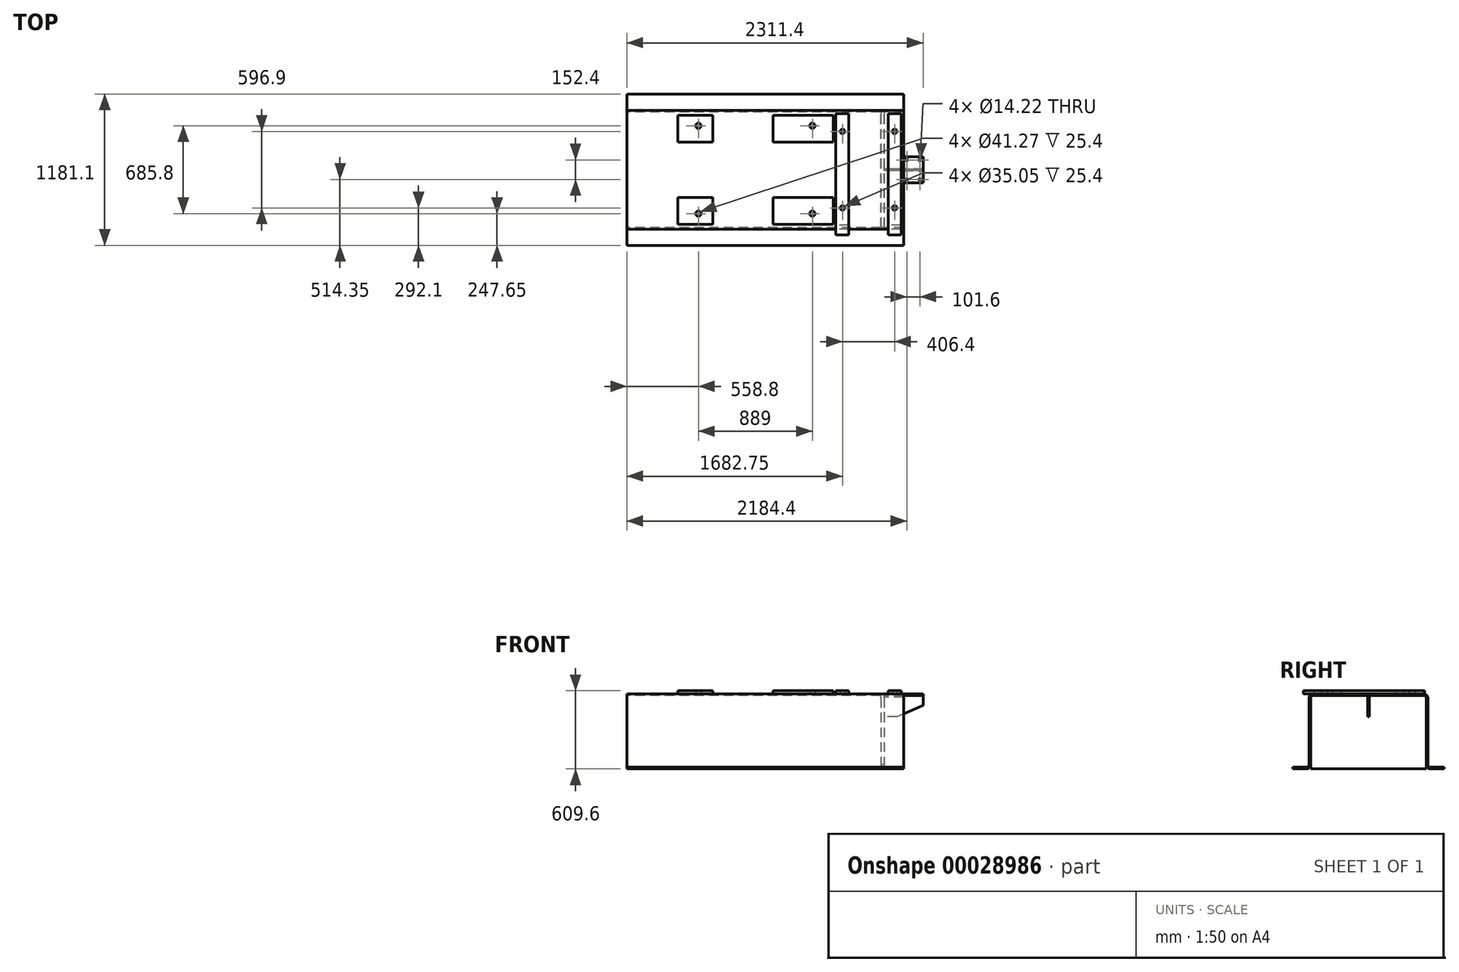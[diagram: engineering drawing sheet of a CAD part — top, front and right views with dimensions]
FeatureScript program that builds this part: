
annotation { "Feature Type Name" : "Feature", "Feature Type Description" : "" }
export const myFeature = defineFeature(function(context is Context, id is Id, definition is map)
    precondition{}
    {
        {
            var Q0;
            Q0=qCreatedBy(makeId("Right.planeOp"),FACE);
            var sketch = newSketch(context, id + "F0", { "sketchPlane" : qUnion([Q0])});
            skLineSegment(sketch, "E0", {"start": v(0, 584.2) * mm, "end": v(0, -94.25) * mm, "construction": true});
            skLineSegment(sketch, "E1", {"start": v(-590.55, 0) * mm, "end": v(129.12, 0) * mm, "construction": true});
            skLineSegment(sketch, "E2.0", {"start": v(-590.55, 88.53) * mm, "end": v(-590.55, -94.25) * mm, "construction": true});
            skPoint(sketch, "E3.orphan", {"position": v(-130.91, 0) * mm});
            skLineSegment(sketch, "E4.0", {"start": v(-590.55, 12.7) * mm, "end": v(129.12, 12.7) * mm, "construction": true});
            skLineSegment(sketch, "E5.0", {"start": v(-590.55, 584.2) * mm, "end": v(129.12, 584.2) * mm, "construction": true});
            skPoint(sketch, "E6.orphan", {"position": v(0, 88.53) * mm});
            skLineSegment(sketch, "E7.0", {"start": v(-463.55, 584.2) * mm, "end": v(-463.55, -94.25) * mm, "construction": true});
            skLineSegment(sketch, "E8.0", {"start": v(-450.85, 584.2) * mm, "end": v(-450.85, -94.25) * mm, "construction": true});
            skLineSegment(sketch, "E9.0", {"start": v(-590.55, 571.5) * mm, "end": v(129.12, 571.5) * mm, "construction": true});
            skLineSegment(sketch, "E10", {"start": v(-590.55, 12.7) * mm, "end": v(-482.6, 12.7) * mm});
            skLineSegment(sketch, "E11", {"start": v(-463.55, 31.75) * mm, "end": v(-463.55, 552.45) * mm});
            skLineSegment(sketch, "E12", {"start": v(0, 584.2) * mm, "end": v(-431.8, 584.2) * mm});
            skLineSegment(sketch, "E13", {"start": v(0, 571.5) * mm, "end": v(-431.8, 571.5) * mm});
            skLineSegment(sketch, "E14", {"start": v(-450.85, 552.45) * mm, "end": v(-450.85, 31.75) * mm});
            skLineSegment(sketch, "E15", {"start": v(-482.6, 0) * mm, "end": v(-590.55, 0) * mm});
            skLineSegment(sketch, "E16", {"start": v(-590.55, 12.7) * mm, "end": v(-590.55, 0) * mm});
            skPoint(sketch, "E17.visualSharp", {"position": v(-463.55, 12.7) * mm});
            skArc(sketch, "E17.filletArc", {"start": v(-482.6, 12.7) * mm, "mid": v(-469.13, 18.28) * mm, "end": v(-463.55, 31.75) * mm});
            skPoint(sketch, "E18.visualSharp", {"position": v(-450.85, 571.5) * mm});
            skArc(sketch, "E18.filletArc", {"start": v(-431.8, 571.5) * mm, "mid": v(-445.27, 565.92) * mm, "end": v(-450.85, 552.45) * mm});
            skPoint(sketch, "E19.visualSharp", {"position": v(-463.55, 584.2) * mm});
            skArc(sketch, "E19.filletArc", {"start": v(-431.8, 584.2) * mm, "mid": v(-454.25, 574.9) * mm, "end": v(-463.55, 552.45) * mm});
            skPoint(sketch, "E20.visualSharp", {"position": v(-450.85, 0) * mm});
            skArc(sketch, "E20.filletArc", {"start": v(-482.6, 0) * mm, "mid": v(-460.15, 9.3) * mm, "end": v(-450.85, 31.75) * mm});
            skArc(sketch, "E21.MirrorCS", {"start": v(431.8, 571.5) * mm, "mid": v(445.27, 565.92) * mm, "end": v(450.85, 552.45) * mm});
            skArc(sketch, "E22.MirrorCS", {"start": v(431.8, 584.2) * mm, "mid": v(454.25, 574.9) * mm, "end": v(463.55, 552.45) * mm});
            skLineSegment(sketch, "E23.MirrorCS", {"start": v(450.85, 577.85) * mm, "end": v(450.85, 31.75) * mm});
            skPoint(sketch, "E24.MirrorP", {"position": v(450.85, 571.5) * mm});
            skLineSegment(sketch, "E25.MirrorCS", {"start": v(0, 584.2) * mm, "end": v(431.8, 584.2) * mm});
            skLineSegment(sketch, "E26.MirrorCS", {"start": v(463.55, 31.75) * mm, "end": v(463.55, 552.45) * mm});
            skLineSegment(sketch, "E27.MirrorCS", {"start": v(0, 571.5) * mm, "end": v(431.8, 571.5) * mm});
            skPoint(sketch, "E28.MirrorP", {"position": v(463.55, 584.2) * mm});
            skLineSegment(sketch, "E29.MirrorCS", {"start": v(450.85, 552.45) * mm, "end": v(450.85, 31.75) * mm});
            skLineSegment(sketch, "E30.MirrorCS", {"start": v(457.2, 571.5) * mm, "end": v(-129.12, 571.5) * mm});
            skLineSegment(sketch, "E31.MirrorCS", {"start": v(590.55, 12.7) * mm, "end": v(590.55, 0) * mm});
            skArc(sketch, "E32.MirrorCS", {"start": v(482.6, 12.7) * mm, "mid": v(469.13, 18.28) * mm, "end": v(463.55, 31.75) * mm});
            skArc(sketch, "E33.MirrorCS", {"start": v(482.6, 0) * mm, "mid": v(460.15, 9.3) * mm, "end": v(450.85, 31.75) * mm});
            skPoint(sketch, "E34.MirrorP", {"position": v(450.85, 0) * mm});
            skPoint(sketch, "E35.MirrorP", {"position": v(463.55, 12.7) * mm});
            skLineSegment(sketch, "E36.MirrorCS", {"start": v(590.55, 0) * mm, "end": v(482.6, 0) * mm});
            skLineSegment(sketch, "E37.MirrorCS", {"start": v(482.6, 0) * mm, "end": v(590.55, 0) * mm});
            skLineSegment(sketch, "E38.MirrorCS", {"start": v(590.55, 88.53) * mm, "end": v(590.55, -94.25) * mm});
            skLineSegment(sketch, "E39.MirrorCS", {"start": v(590.55, 12.7) * mm, "end": v(482.6, 12.7) * mm});
            skLineSegment(sketch, "E40.MirrorCS", {"start": v(463.55, 552.45) * mm, "end": v(463.55, 31.75) * mm});
            skLineSegment(sketch, "E41.MirrorCS", {"start": v(590.55, 12.7) * mm, "end": v(463.55, 12.7) * mm});
            skLineSegment(sketch, "E42.MirrorCS", {"start": v(450.85, 584.2) * mm, "end": v(450.85, 31.75) * mm});
            skLineSegment(sketch, "E43.trimOffspring", {"start": v(129.12, 12.7) * mm, "end": v(-129.12, 12.7) * mm});
            skLineSegment(sketch, "E44.trimOffspring", {"start": v(463.55, 12.7) * mm, "end": v(463.55, 6.35) * mm});
            skLineSegment(sketch, "E45.trimOffspring", {"start": v(129.12, 0) * mm, "end": v(-129.12, 0) * mm});
            skPoint(sketch, "E46.trimOffspring.end.orphan", {"position": v(463.55, -94.25) * mm});
            skPoint(sketch, "E47.trimOffspring.end.orphan", {"position": v(450.85, -94.25) * mm});
            skLineSegment(sketch, "E48.trimOffspring", {"start": v(431.8, 584.2) * mm, "end": v(-129.12, 584.2) * mm});
            skPoint(sketch, "E49.orphan", {"position": v(450.85, 584.2) * mm});
            skPoint(sketch, "E50.orphan", {"position": v(590.55, 571.5) * mm});
            skLineSegment(sketch, "E51.trimOffspring", {"start": v(463.55, 552.45) * mm, "end": v(463.55, 6.35) * mm});
            skPoint(sketch, "E52.MirrorCS.start.orphan", {"position": v(590.55, 584.2) * mm});
            skSolve(sketch);
        }
        {
            var Q0;
            Q0 = qSketchRegion(id + "F0", true);
            extrude(context, id + "F1", {"entities" : qUnion([Q0]), "endBound" : BoundingType.SYMMETRIC, "depth" : 2159 * mm});
        }
        {
            var Q0;
            Q0=makeQuery(id+"F1.opExtrude","SWEPT_FACE",FACE,{"disambiguationData":[OSD([sQuery(id+"F0.wireOp",EDGE,"E12"),sQuery(id+"F0.wireOp",EDGE,"E48.trimOffspring")])]});
            var sketch = newSketch(context, id + "F2", { "sketchPlane" : qUnion([Q0])});
            skLineSegment(sketch, "E53", {"start": v(-1403.71, 0) * mm, "end": v(1616.58, 0) * mm, "construction": true});
            skLineSegment(sketch, "E54.0", {"start": v(-1403.71, 215.9) * mm, "end": v(1616.58, 215.9) * mm, "construction": true});
            skLineSegment(sketch, "E55.0", {"start": v(-1403.71, 425.45) * mm, "end": v(1616.58, 425.45) * mm, "construction": true});
            skLineSegment(sketch, "E56.0", {"start": v(806.45, 431.8) * mm, "end": v(806.45, -431.8) * mm, "construction": true});
            skLineSegment(sketch, "E57.0", {"start": v(-76.2, 431.8) * mm, "end": v(-76.2, -431.8) * mm, "construction": true});
            skLineSegment(sketch, "E58.0", {"start": v(60.45, 431.8) * mm, "end": v(60.45, -431.8) * mm, "construction": true});
            skLineSegment(sketch, "E59.0", {"start": v(530.35, 431.8) * mm, "end": v(530.35, -431.8) * mm, "construction": true});
            skLineSegment(sketch, "E60.0", {"start": v(-409.45, 431.8) * mm, "end": v(-409.45, -431.8) * mm, "construction": true});
            skLineSegment(sketch, "E61.0", {"start": v(-682.5, 431.8) * mm, "end": v(-682.5, -431.8) * mm, "construction": true});
            skLineSegment(sketch, "E62.bottom", {"start": v(-682.5, 425.45) * mm, "end": v(-409.45, 425.45) * mm});
            skLineSegment(sketch, "E62.top", {"start": v(-682.5, 215.9) * mm, "end": v(-409.45, 215.9) * mm});
            skLineSegment(sketch, "E62.left", {"start": v(-682.5, 425.45) * mm, "end": v(-682.5, 215.9) * mm});
            skLineSegment(sketch, "E62.right", {"start": v(-409.45, 425.45) * mm, "end": v(-409.45, 215.9) * mm});
            skLineSegment(sketch, "E63.bottom", {"start": v(530.35, 425.45) * mm, "end": v(60.45, 425.45) * mm});
            skLineSegment(sketch, "E63.top", {"start": v(530.35, 215.9) * mm, "end": v(60.45, 215.9) * mm});
            skLineSegment(sketch, "E63.left", {"start": v(530.35, 425.45) * mm, "end": v(530.35, 215.9) * mm});
            skLineSegment(sketch, "E63.right", {"start": v(60.45, 425.45) * mm, "end": v(60.45, 215.9) * mm});
            skLineSegment(sketch, "E64.0", {"start": v(-520.7, 431.8) * mm, "end": v(-520.7, -431.8) * mm, "construction": true});
            skLineSegment(sketch, "E65.0", {"start": v(-1403.71, 342.9) * mm, "end": v(1616.58, 342.9) * mm, "construction": true});
            skLineSegment(sketch, "E66.MirrorCS", {"start": v(368.3, 431.8) * mm, "end": v(368.3, -431.8) * mm, "construction": true});
            skCircle(sketch, "E67", {"center": v(-520.7, 342.9) * mm, "radius": 20.64 * mm});
            skCircle(sketch, "E68", {"center": v(368.3, 342.9) * mm, "radius": 20.64 * mm});
            skCircle(sketch, "E69.MirrorC", {"center": v(-520.7, -342.9) * mm, "radius": 20.64 * mm});
            skCircle(sketch, "E70.MirrorC", {"center": v(368.3, -342.9) * mm, "radius": 20.64 * mm});
            skLineSegment(sketch, "E71.MirrorCS", {"start": v(-682.5, -425.45) * mm, "end": v(-409.45, -425.45) * mm});
            skLineSegment(sketch, "E72.MirrorCS", {"start": v(-682.5, -215.9) * mm, "end": v(-409.45, -215.9) * mm});
            skLineSegment(sketch, "E73.MirrorCS", {"start": v(530.35, -425.45) * mm, "end": v(530.35, -215.9) * mm});
            skLineSegment(sketch, "E74.MirrorCS", {"start": v(-682.5, -425.45) * mm, "end": v(-682.5, -215.9) * mm});
            skLineSegment(sketch, "E75.MirrorCS", {"start": v(-409.45, -425.45) * mm, "end": v(-409.45, -215.9) * mm});
            skLineSegment(sketch, "E76.MirrorCS", {"start": v(60.45, -425.45) * mm, "end": v(60.45, -215.9) * mm});
            skLineSegment(sketch, "E77.MirrorCS", {"start": v(530.35, -425.45) * mm, "end": v(60.45, -425.45) * mm});
            skLineSegment(sketch, "E78.MirrorCS", {"start": v(530.35, -215.9) * mm, "end": v(60.45, -215.9) * mm});
            skSolve(sketch);
        }
        {
            var Q0;
            Q0 = qSketchRegion(id + "F2", true);
            extrude(context, id + "F3", {"entities" : qUnion([Q0]), "operationType" : NewBodyOperationType.ADD, "depth" : 25.4 * mm});
        }
        {
            var Q0;
            Q0=makeQuery(id+"F2.imprint","IMPRINT",FACE,{"disambiguationData":[TD([[makeQuery(id+"F2.imprint","IMPRINT",EDGE,{"derivedFrom":sQuery(id+"F2.wireOp",EDGE,"E62.bottom")}),1.0]])]});
            var sketch = newSketch(context, id + "F4", { "sketchPlane" : qUnion([Q0])});
            skLineSegment(sketch, "E79.0", {"start": v(806.45, 438.15) * mm, "end": v(806.45, -431.8) * mm, "construction": true});
            skLineSegment(sketch, "E80.0", {"start": v(-1403.71, 0) * mm, "end": v(1616.58, 0) * mm, "construction": true});
            skLineSegment(sketch, "E81.0", {"start": v(652.53, 438.15) * mm, "end": v(652.53, -508) * mm, "construction": true});
            skLineSegment(sketch, "E82.0", {"start": v(550.93, 431.8) * mm, "end": v(550.93, -508) * mm, "construction": true});
            skLineSegment(sketch, "E83.0", {"start": v(-1403.71, -508) * mm, "end": v(1616.58, -508) * mm, "construction": true});
            skLineSegment(sketch, "E84.0", {"start": v(-1403.71, 438.15) * mm, "end": v(1616.58, 438.15) * mm, "construction": true});
            skPoint(sketch, "E85.orphan", {"position": v(806.45, 431.8) * mm});
            skLineSegment(sketch, "E86.bottom", {"start": v(652.53, 438.15) * mm, "end": v(550.93, 438.15) * mm});
            skLineSegment(sketch, "E86.top", {"start": v(652.53, -508) * mm, "end": v(550.93, -508) * mm});
            skLineSegment(sketch, "E86.left", {"start": v(652.53, 438.15) * mm, "end": v(652.53, -508) * mm});
            skLineSegment(sketch, "E86.right", {"start": v(550.93, 438.15) * mm, "end": v(550.93, -508) * mm});
            skLineSegment(sketch, "E87.MirrorCS", {"start": v(960.37, 438.15) * mm, "end": v(960.37, -508) * mm});
            skLineSegment(sketch, "E88.MirrorCS", {"start": v(1061.97, 431.8) * mm, "end": v(1061.97, -508) * mm});
            skLineSegment(sketch, "E89.MirrorCS", {"start": v(1061.97, 438.15) * mm, "end": v(1061.97, -508) * mm});
            skLineSegment(sketch, "E90.MirrorCS", {"start": v(960.37, -508) * mm, "end": v(1061.97, -508) * mm});
            skLineSegment(sketch, "E91.MirrorCS", {"start": v(960.37, 438.15) * mm, "end": v(1061.97, 438.15) * mm});
            skLineSegment(sketch, "E92.0", {"start": v(603.25, 438.15) * mm, "end": v(603.25, -431.8) * mm, "construction": true});
            skLineSegment(sketch, "E93.0", {"start": v(-1403.71, -298.45) * mm, "end": v(1616.58, -298.45) * mm, "construction": true});
            skCircle(sketch, "E94", {"center": v(603.25, -298.45) * mm, "radius": 17.53 * mm});
            skCircle(sketch, "E95.MirrorC", {"center": v(603.25, 298.45) * mm, "radius": 17.53 * mm});
            skCircle(sketch, "E96.MirrorC", {"center": v(1009.65, 298.45) * mm, "radius": 17.53 * mm});
            skCircle(sketch, "E97.MirrorC", {"center": v(1009.65, -298.45) * mm, "radius": 17.53 * mm});
            skSolve(sketch);
        }
        {
            var Q0;
            Q0 = qSketchRegion(id + "F4", true);
            extrude(context, id + "F5", {"entities" : qUnion([Q0]), "operationType" : NewBodyOperationType.ADD, "depth" : 25.4 * mm});
        }
        {
            var Q0;
            Q0=makeQuery(id+"F1.opExtrude","CAP_FACE",FACE,{"disambiguationData":[OSD([sQuery(id+"F0.wireOp",EDGE,"E10"),sQuery(id+"F0.wireOp",EDGE,"E11"),sQuery(id+"F0.wireOp",EDGE,"E12"),sQuery(id+"F0.wireOp",EDGE,"E13"),sQuery(id+"F0.wireOp",EDGE,"E14"),sQuery(id+"F0.wireOp",EDGE,"E15"),sQuery(id+"F0.wireOp",EDGE,"E16"),sQuery(id+"F0.wireOp",EDGE,"E17.filletArc"),sQuery(id+"F0.wireOp",EDGE,"E18.filletArc"),sQuery(id+"F0.wireOp",EDGE,"E19.filletArc"),sQuery(id+"F0.wireOp",EDGE,"E20.filletArc"),sQuery(id+"F0.wireOp",EDGE,"E21.MirrorCS"),sQuery(id+"F0.wireOp",EDGE,"E22.MirrorCS"),sQuery(id+"F0.wireOp",EDGE,"E30.MirrorCS"),sQuery(id+"F0.wireOp",EDGE,"E32.MirrorCS"),sQuery(id+"F0.wireOp",EDGE,"E33.MirrorCS"),sQuery(id+"F0.wireOp",EDGE,"E37.MirrorCS"),sQuery(id+"F0.wireOp",EDGE,"E38.MirrorCS"),sQuery(id+"F0.wireOp",EDGE,"E41.MirrorCS"),sQuery(id+"F0.wireOp",EDGE,"E42.MirrorCS"),sQuery(id+"F0.wireOp",EDGE,"E48.trimOffspring"),sQuery(id+"F0.wireOp",EDGE,"E51.trimOffspring")])],"isStart":false});
            cPlane(context, id + "F6", {"entities" : qUnion([Q0]), "cplaneType" : CPlaneType.OFFSET, "offset" : 152.4 * mm, "oppositeDirection" : true, "width" : 152.4 * mm, "height" : 152.4 * mm});
        }
        {
            var Q0;
            Q0=qCreatedBy(id+"F6.planeOp",FACE);
            var sketch = newSketch(context, id + "F7", { "sketchPlane" : qUnion([Q0])});
            skLineSegment(sketch, "E98.1", {"start": v(-450.85, 552.45) * mm, "end": v(-450.85, 0) * mm});
            skLineSegment(sketch, "E98.2", {"start": v(431.8, 571.5) * mm, "end": v(-431.8, 571.5) * mm});
            skLineSegment(sketch, "E99.1", {"start": v(-450.85, 552.45) * mm, "end": v(-450.85, 31.75) * mm});
            skLineSegment(sketch, "E100.0", {"start": v(450.85, 552.45) * mm, "end": v(450.85, 0) * mm});
            skArc(sketch, "E101.0", {"start": v(431.8, 571.5) * mm, "mid": v(445.27, 565.92) * mm, "end": v(450.85, 552.45) * mm});
            skArc(sketch, "E102.0", {"start": v(-431.8, 571.5) * mm, "mid": v(-445.27, 565.92) * mm, "end": v(-450.85, 552.45) * mm});
            skLineSegment(sketch, "E103.0", {"start": v(-482.6, 0) * mm, "end": v(-590.55, 0) * mm, "construction": true});
            skLineSegment(sketch, "E104.0", {"start": v(482.6, 0) * mm, "end": v(590.55, 0) * mm, "construction": true});
            skLineSegment(sketch, "E105", {"start": v(-482.6, 0) * mm, "end": v(482.6, 0) * mm});
            skPoint(sketch, "E106.orphan", {"position": v(450.85, 31.75) * mm});
            skSolve(sketch);
        }
        {
            var Q0;
            Q0 = qSketchRegion(id + "F7", true);
            extrude(context, id + "F8", {"entities" : qUnion([Q0]), "operationType" : NewBodyOperationType.ADD, "oppositeDirection" : true, "depth" : 25.4 * mm});
        }
        {
            var Q0;
            {var subQ0=sQuery(id+"F0.wireOp",EDGE,"E12");var subQ1=sQuery(id+"F0.wireOp",EDGE,"E48.trimOffspring");var subQ4=sQuery(id+"F0.wireOp",EDGE,"E19.filletArc");var subQ5=makeQuery(id+"F1.opExtrude","SWEPT_FACE",FACE,{"disambiguationData":[OSD([subQ4])]});var subQ25=sQuery(id+"F4.wireOp",EDGE,"E86.left");Q0=makeQuery(id+"F5.boolean.opBoolean","SPLIT",FACE,{"disambiguationData":[TD([makeQuery(id+"F5.opExtrude","SWEPT_FACE",FACE,{"disambiguationData":[OSD([subQ25])]})])],"derivedFrom":makeQuery(id+"F3.boolean.opBoolean","SPLIT",FACE,{"disambiguationData":[TD([subQ5])],"derivedFrom":makeQuery(id+"F1.opExtrude","SWEPT_FACE",FACE,{"disambiguationData":[OSD([subQ0,subQ1])]})})});}
            var sketch = newSketch(context, id + "F9", { "sketchPlane" : qUnion([Q0])});
            skLineSegment(sketch, "E107", {"start": v(0, 0) * mm, "end": v(1648.56, 0) * mm, "construction": true});
            skLineSegment(sketch, "E108.0", {"start": v(1079.5, 431.8) * mm, "end": v(1079.5, -431.8) * mm});
            skLineSegment(sketch, "E109.0", {"start": v(1231.9, 431.8) * mm, "end": v(1231.9, -431.8) * mm});
            skLineSegment(sketch, "E110.0", {"start": v(0, 101.6) * mm, "end": v(1648.56, 101.6) * mm});
            skLineSegment(sketch, "E111.0", {"start": v(0, -101.6) * mm, "end": v(1648.56, -101.6) * mm});
            skSolve(sketch);
        }
        {
            var Q0;
            Q0 = qSketchRegion(id + "F9", true);
            extrude(context, id + "F10", {"entities" : qUnion([Q0]), "oppositeDirection" : true, "depth" : 12.7 * mm});
        }
        {
            var Q0;
            Q0=qCreatedBy(makeId("Front.planeOp"),FACE);
            var sketch = newSketch(context, id + "F11", { "sketchPlane" : qUnion([Q0])});
            skLineSegment(sketch, "E112.0", {"start": v(1079.5, 571.5) * mm, "end": v(1231.9, 571.5) * mm});
            skLineSegment(sketch, "E113.0", {"start": v(927.1, 552.45) * mm, "end": v(927.1, 31.75) * mm});
            skLineSegment(sketch, "E114.0", {"start": v(1079.5, 571.5) * mm, "end": v(927.1, 571.5) * mm});
            skLineSegment(sketch, "E115.0", {"start": v(1079.5, 558.8) * mm, "end": v(927.1, 558.8) * mm});
            skLineSegment(sketch, "E115.1", {"start": v(1079.5, 558.8) * mm, "end": v(1231.9, 558.8) * mm});
            skLineSegment(sketch, "E116.0", {"start": v(1079.5, 406.4) * mm, "end": v(926.76, 406.4) * mm});
            skLineSegment(sketch, "E116.1", {"start": v(1079.5, 406.4) * mm, "end": v(1231.9, 406.4) * mm});
            skLineSegment(sketch, "E117", {"start": v(1231.9, 571.5) * mm, "end": v(1231.9, 558.8) * mm});
            skLineSegment(sketch, "E118", {"start": v(1231.9, 558.8) * mm, "end": v(1231.9, 495.3) * mm});
            skLineSegment(sketch, "E119", {"start": v(1231.9, 495.3) * mm, "end": v(1028.36, 406.4) * mm});
            skLineSegment(sketch, "E120", {"start": v(1079.5, 571.5) * mm, "end": v(1079.5, 558.8) * mm});
            skLineSegment(sketch, "E121", {"start": v(927.1, 558.8) * mm, "end": v(927.1, 552.45) * mm});
            skSolve(sketch);
        }
        {
            var Q0;
            Q0 = qSketchRegion(id + "F11", true);
            extrude(context, id + "F12", {"entities" : qUnion([Q0]), "endBound" : BoundingType.SYMMETRIC, "depth" : 12.7 * mm});
        }
        {
            var Q0;
            Q0=makeQuery(id+"F12.opExtrude","SWEPT_BODY",BODY,{"disambiguationData":[OSD([sQuery(id+"F11.wireOp",EDGE,"E112.0"),sQuery(id+"F11.wireOp",EDGE,"E113.0"),sQuery(id+"F11.wireOp",EDGE,"E115.0"),sQuery(id+"F11.wireOp",EDGE,"E116.0"),sQuery(id+"F11.wireOp",EDGE,"E117"),sQuery(id+"F11.wireOp",EDGE,"E118"),sQuery(id+"F11.wireOp",EDGE,"E119"),sQuery(id+"F11.wireOp",EDGE,"E120"),sQuery(id+"F11.wireOp",EDGE,"E121")])]});
            var Q1;
            Q1=makeQuery(id+"F10.opExtrude","SWEPT_BODY",BODY,{"disambiguationData":[OSD([sQuery(id+"F9.wireOp",EDGE,"E108.0"),sQuery(id+"F9.wireOp",EDGE,"E109.0"),sQuery(id+"F9.wireOp",EDGE,"E110.0"),sQuery(id+"F9.wireOp",EDGE,"E111.0")])]});
            booleanBodies(context, id + "F13", {"operationType" : BooleanOperationType.UNION, "tools" : qUnion([Q0, Q1])});
        }
        {
            var Q0;
            Q0=makeQuery(id+"F10.opExtrude","CAP_FACE",FACE,{"disambiguationData":[OSD([sQuery(id+"F9.wireOp",EDGE,"E108.0"),sQuery(id+"F9.wireOp",EDGE,"E109.0"),sQuery(id+"F9.wireOp",EDGE,"E110.0"),sQuery(id+"F9.wireOp",EDGE,"E111.0")])],"isStart":true});
            var sketch = newSketch(context, id + "F14", { "sketchPlane" : qUnion([Q0])});
            skLineSegment(sketch, "E122.0", {"start": v(1206.5, 76.2) * mm, "end": v(1104.9, 76.2) * mm, "construction": true});
            skLineSegment(sketch, "E122.1", {"start": v(1206.5, -76.2) * mm, "end": v(1206.5, 76.2) * mm, "construction": true});
            skLineSegment(sketch, "E122.2", {"start": v(1104.9, -76.2) * mm, "end": v(1206.5, -76.2) * mm, "construction": true});
            skLineSegment(sketch, "E122.3", {"start": v(1104.9, 76.2) * mm, "end": v(1104.9, -76.2) * mm, "construction": true});
            skPoint(sketch, "E123", {"position": v(1104.9, 76.2) * mm});
            skPoint(sketch, "E124", {"position": v(1206.5, 76.2) * mm});
            skPoint(sketch, "E125", {"position": v(1206.5, -76.2) * mm});
            skPoint(sketch, "E126", {"position": v(1104.9, -76.2) * mm});
            skSolve(sketch);
        }
        {
            var Q0;
            Q0=sQuery(id+"F14.wireOp",VERTEX,"E123");
            var Q1;
            Q1=sQuery(id+"F14.wireOp",VERTEX,"E124");
            var Q2;
            Q2=sQuery(id+"F14.wireOp",VERTEX,"E126");
            var Q3;
            Q3=sQuery(id+"F14.wireOp",VERTEX,"E125");
            var Q4;
            Q4=makeQuery(id+"F12.opExtrude","SWEPT_BODY",BODY,{"disambiguationData":[OSD([sQuery(id+"F11.wireOp",EDGE,"E112.0"),sQuery(id+"F11.wireOp",EDGE,"E113.0"),sQuery(id+"F11.wireOp",EDGE,"E115.0"),sQuery(id+"F11.wireOp",EDGE,"E116.0"),sQuery(id+"F11.wireOp",EDGE,"E117"),sQuery(id+"F11.wireOp",EDGE,"E118"),sQuery(id+"F11.wireOp",EDGE,"E119"),sQuery(id+"F11.wireOp",EDGE,"E120"),sQuery(id+"F11.wireOp",EDGE,"E121")])]});
            hole(context, id + "F15", {"style" : HoleStyle.SIMPLE, "holeDiameter" : 14.22 * mm, "endStyle" : HoleEndStyle.THROUGH, "locations" : qUnion([Q0, Q1, Q2, Q3]), "scope" : qUnion([Q4])});
        }
    });
